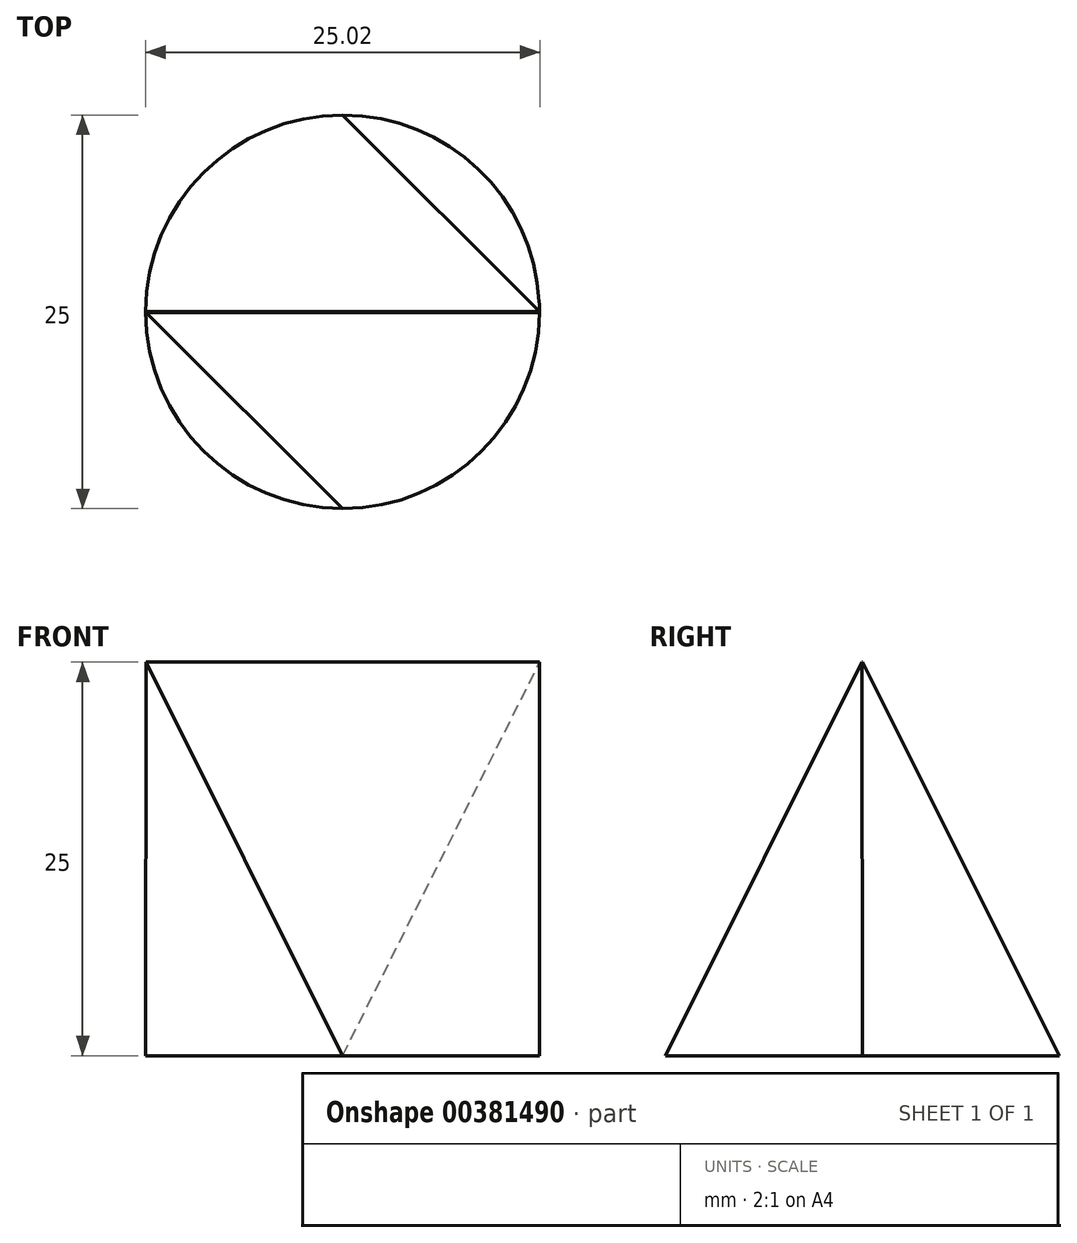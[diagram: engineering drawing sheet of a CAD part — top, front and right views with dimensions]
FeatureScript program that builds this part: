
annotation { "Feature Type Name" : "Feature", "Feature Type Description" : "" }
export const myFeature = defineFeature(function(context is Context, id is Id, definition is map)
    precondition{}
    {
        {
            var Q0;
            Q0=qCreatedBy(makeId("Top.planeOp"),FACE);
            var sketch = newSketch(context, id + "F0", { "sketchPlane" : qUnion([Q0])});
            skCircle(sketch, "E0", {"center": v(0, 0) * mm, "radius": 12.5 * mm});
            skSolve(sketch);
        }
        {
            var Q0;
            Q0=qCreatedBy(makeId("Top.planeOp"),FACE);
            cPlane(context, id + "F1", {"entities" : qUnion([Q0]), "cplaneType" : CPlaneType.OFFSET, "offset" : 25 * mm, "width" : 150 * mm, "height" : 150 * mm});
        }
        {
            var Q0;
            Q0=qCreatedBy(id+"F1.planeOp",FACE);
            var sketch = newSketch(context, id + "F2", { "sketchPlane" : qUnion([Q0])});
            skLineSegment(sketch, "E1.bottom", {"start": v(-12.48, 0) * mm, "end": v(12.52, 0) * mm});
            skLineSegment(sketch, "E1.top", {"start": v(-12.48, -0.05) * mm, "end": v(12.52, -0.05) * mm});
            skLineSegment(sketch, "E1.left", {"start": v(-12.48, 0) * mm, "end": v(-12.48, -0.05) * mm});
            skLineSegment(sketch, "E1.right", {"start": v(12.52, 0) * mm, "end": v(12.52, -0.05) * mm});
            skSolve(sketch);
        }
        {
            var Q0;
            Q0=makeQuery(id+"F0.imprint","IMPRINT",FACE,{"disambiguationData":[TD([[makeQuery(id+"F0.imprint","IMPRINT",EDGE,{"derivedFrom":sQuery(id+"F0.wireOp",EDGE,"E0")}),1.0]])]});
            var Q1;
            Q1=makeQuery(id+"F2.imprint","IMPRINT",FACE,{"disambiguationData":[TD([[makeQuery(id+"F2.imprint","IMPRINT",EDGE,{"derivedFrom":sQuery(id+"F2.wireOp",EDGE,"E1.bottom")}),-1.0]])]});
            loft(context, id + "F3", {"sheetProfilesArray" : [{ "sheetProfileEntities" : qUnion([Q0]) }, { "sheetProfileEntities" : qUnion([Q1]) }]});
        }
    });
